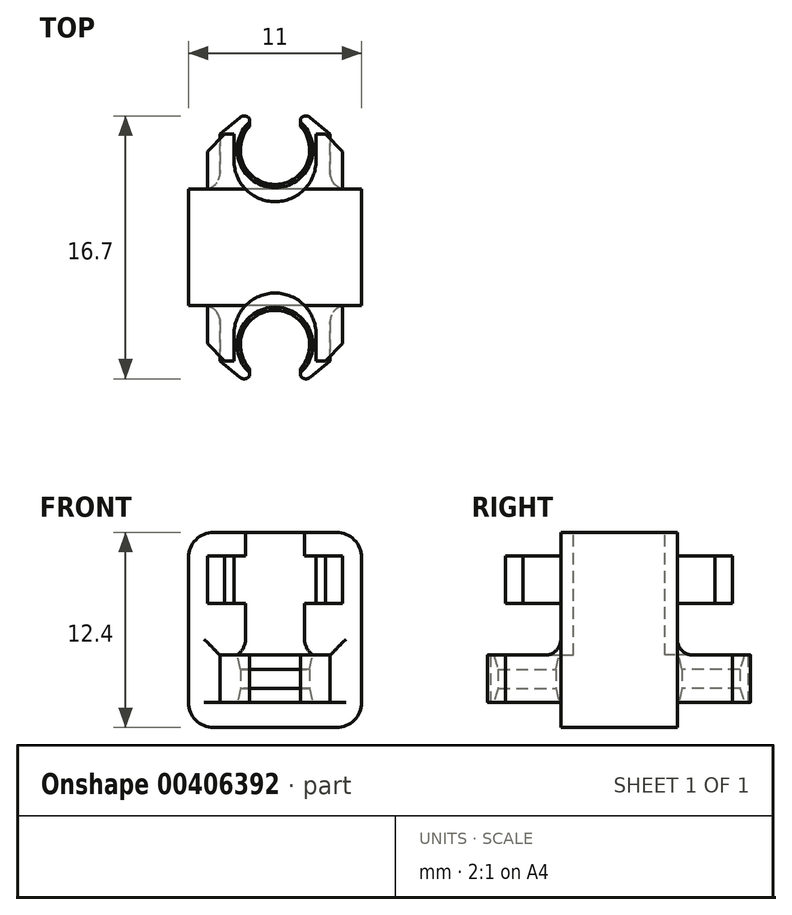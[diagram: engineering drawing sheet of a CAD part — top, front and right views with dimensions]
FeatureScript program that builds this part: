
annotation { "Feature Type Name" : "Feature", "Feature Type Description" : "" }
export const myFeature = defineFeature(function(context is Context, id is Id, definition is map)
    precondition{}
    {
        {
            var Q0;
            Q0=qCreatedBy(makeId("Top.planeOp"),FACE);
            var sketch = newSketch(context, id + "F0", { "sketchPlane" : qUnion([Q0])});
            skArc(sketch, "E0", {"start": v(-1.63, 1.48) * mm, "mid": v(-2.01, -0.9) * mm, "end": v(0, -2.2) * mm});
            skLineSegment(sketch, "E1", {"start": v(-1.63, 1.98) * mm, "end": v(-1.9, 2.31) * mm});
            skLineSegment(sketch, "E2", {"start": v(-1.9, 2.31) * mm, "end": v(-3.5, 1) * mm});
            skLineSegment(sketch, "E3", {"start": v(-5.5, -2.5) * mm, "end": v(-5.5, -6.2) * mm});
            skLineSegment(sketch, "E4", {"start": v(-5.5, -6.2) * mm, "end": v(0, -6.2) * mm});
            skLineSegment(sketch, "E5", {"start": v(0, -6.2) * mm, "end": v(0, -2.2) * mm});
            skLineSegment(sketch, "E6", {"start": v(-3.5, 1) * mm, "end": v(-3.5, -2.5) * mm});
            skLineSegment(sketch, "E7", {"start": v(-3.5, -2.5) * mm, "end": v(-5.5, -2.5) * mm});
            skLineSegment(sketch, "E8", {"start": v(-1.63, 1.98) * mm, "end": v(-1.63, 1.48) * mm});
            skPoint(sketch, "E8.endSnap0", {"position": v(-1.65, 2) * mm});
            skPoint(sketch, "E9.orphan", {"position": v(-1.4, 1.7) * mm});
            skSolve(sketch);
        }
        {
            var Q0;
            Q0 = qSketchRegion(id + "F0", true);
            extrude(context, id + "F1", {"entities" : qUnion([Q0]), "depth" : 12.4 * mm, "offsetDistance" : 25 * mm});
        }
        {
            var Q0;
            Q0=makeQuery(id+"F1.opExtrude","SWEPT_FACE",FACE,{"disambiguationData":[OSD([sQuery(id+"F0.wireOp",EDGE,"E6")])]});
            var sketch = newSketch(context, id + "F2", { "sketchPlane" : qUnion([Q0])});
            skLineSegment(sketch, "E10.bottom", {"start": v(2.5, 7.9) * mm, "end": v(-2.31, 7.9) * mm});
            skLineSegment(sketch, "E10.top", {"start": v(2.5, 4.6) * mm, "end": v(-2.31, 4.6) * mm});
            skLineSegment(sketch, "E10.left", {"start": v(2.5, 7.9) * mm, "end": v(2.5, 4.6) * mm});
            skLineSegment(sketch, "E10.right", {"start": v(-2.31, 7.9) * mm, "end": v(-2.31, 4.6) * mm});
            skLineSegment(sketch, "E11.bottom", {"start": v(-2.31, 0) * mm, "end": v(2.5, 0) * mm});
            skLineSegment(sketch, "E11.top", {"start": v(-2.31, 1.6) * mm, "end": v(2.5, 1.6) * mm});
            skLineSegment(sketch, "E11.left", {"start": v(-2.31, 0) * mm, "end": v(-2.31, 1.6) * mm});
            skLineSegment(sketch, "E11.right", {"start": v(2.5, 0) * mm, "end": v(2.5, 1.6) * mm});
            skLineSegment(sketch, "E12.bottom", {"start": v(2.5, 10.9) * mm, "end": v(-2.31, 10.9) * mm});
            skLineSegment(sketch, "E12.top", {"start": v(2.5, 12.4) * mm, "end": v(-2.31, 12.4) * mm});
            skLineSegment(sketch, "E12.left", {"start": v(2.5, 10.9) * mm, "end": v(2.5, 12.4) * mm});
            skLineSegment(sketch, "E12.right", {"start": v(-2.31, 10.9) * mm, "end": v(-2.31, 12.4) * mm});
            skSolve(sketch);
        }
        {
            var Q0;
            Q0 = qSketchRegion(id + "F2", true);
            extrude(context, id + "F3", {"entities" : qUnion([Q0]), "operationType" : NewBodyOperationType.REMOVE, "oppositeDirection" : true, "depth" : 25 * mm, "offsetDistance" : 25 * mm});
        }
        {
            var Q0;
            Q0=makeQuery(id+"F1.opExtrude","CAP_FACE",FACE,{"disambiguationData":[OSD([sQuery(id+"F0.wireOp",EDGE,"E0"),sQuery(id+"F0.wireOp",EDGE,"E1"),sQuery(id+"F0.wireOp",EDGE,"E2"),sQuery(id+"F0.wireOp",EDGE,"E3"),sQuery(id+"F0.wireOp",EDGE,"E4"),sQuery(id+"F0.wireOp",EDGE,"E5"),sQuery(id+"F0.wireOp",EDGE,"E6"),sQuery(id+"F0.wireOp",EDGE,"E7")])],"isStart":false});
            var sketch = newSketch(context, id + "F4", { "sketchPlane" : qUnion([Q0])});
            skLineSegment(sketch, "E13", {"start": v(-2.6, -0.7) * mm, "end": v(-2.6, 1) * mm});
            skLineSegment(sketch, "E14", {"start": v(-3.5, 1) * mm, "end": v(-2.6, 1) * mm});
            skArc(sketch, "E15", {"start": v(-2.6, -0.7) * mm, "mid": v(-1.84, -2.54) * mm, "end": v(0, -3.3) * mm});
            skLineSegment(sketch, "E16.0", {"start": v(-1.9, 2.31) * mm, "end": v(-3.5, 1) * mm});
            skLineSegment(sketch, "E16.1", {"start": v(-1.63, 1.98) * mm, "end": v(-1.9, 2.31) * mm});
            skLineSegment(sketch, "E17.0", {"start": v(-1.63, 1.98) * mm, "end": v(-1.63, 1.48) * mm});
            skArc(sketch, "E18.0", {"start": v(-1.63, 1.48) * mm, "mid": v(-2.01, -0.9) * mm, "end": v(0, -2.2) * mm});
            skPoint(sketch, "E19.endSnap0", {"position": v(-2.6, 0.15) * mm});
            skLineSegment(sketch, "E20", {"start": v(0, -3.3) * mm, "end": v(0, -2.2) * mm});
            skSolve(sketch);
        }
        {
            var Q0;
            Q0 = qSketchRegion(id + "F4", true);
            var Q1;
            Q1=makeQuery(id+"F3.boolean.opBoolean","COPY",FACE,{"derivedFrom":makeQuery(id+"F3.opExtrude","SWEPT_FACE",FACE,{"disambiguationData":[OSD([sQuery(id+"F2.wireOp",EDGE,"E10.top")])]})});
            extrude(context, id + "F5", {"entities" : qUnion([Q0]), "operationType" : NewBodyOperationType.REMOVE, "endBound" : BoundingType.UP_TO_SURFACE, "oppositeDirection" : true, "depth" : 25 * mm, "endBoundEntityFace" : qUnion([Q1]), "offsetDistance" : 25 * mm});
        }
        {
            var Q0;
            Q0=makeQuery(id+"F3.boolean.opBoolean","SPLIT",FACE,{"disambiguationData":[TD([makeQuery(id+"F3.opExtrude","SWEPT_FACE",FACE,{"disambiguationData":[OSD([sQuery(id+"F2.wireOp",EDGE,"E10.bottom")])]})])],"derivedFrom":makeQuery(id+"F1.opExtrude","SWEPT_FACE",FACE,{"disambiguationData":[OSD([sQuery(id+"F0.wireOp",EDGE,"E6")])]})});
            extrude(context, id + "F6", {"entities" : qUnion([Q0]), "operationType" : NewBodyOperationType.ADD, "depth" : 0.8 * mm, "offsetDistance" : 25 * mm});
        }
        {
            var Q0;
            Q0=makeQuery(id+"F6.opExtrude","CAP_EDGE",EDGE,{"disambiguationData":[OSD([sQuery(id+"F0.wireOp",EDGE,"E2"),sQuery(id+"F0.wireOp",EDGE,"E6"),sQuery(id+"F4.wireOp",EDGE,"E14"),sQuery(id+"F4.wireOp",EDGE,"E16.0")])],"isStart":false});
            chamfer(context, id + "F7", {"entities" : qUnion([Q0]), "width" : 1.1 * mm, "tangentPropagation" : true});
        }
        {
            var Q0;
            {var subQ0=sQuery(id+"F0.wireOp",EDGE,"E2");var subQ1=sQuery(id+"F0.wireOp",EDGE,"E1");Q0=makeQuery(id+"F3.boolean.opBoolean","SPLIT",EDGE,{"disambiguationData":[TD([makeQuery(id+"F3.opExtrude","SWEPT_FACE",FACE,{"disambiguationData":[OSD([sQuery(id+"F2.wireOp",EDGE,"E10.top")])]})])],"derivedFrom":makeQuery(id+"F1.opExtrude","SWEPT_EDGE",EDGE,{"disambiguationData":[OSD([subQ1,subQ0])]})});}
            fillet(context, id + "F8", {"entities" : qUnion([Q0]), "radius" : 0.4 * mm, "tangentPropagation" : true, "allowEdgeOverflow" : false});
        }
        {
            var Q0;
            {var subQ0=sQuery(id+"F0.wireOp",EDGE,"E7");var subQ1=sQuery(id+"F0.wireOp",EDGE,"E6");Q0=makeQuery(id+"F3.boolean.opBoolean","SPLIT",EDGE,{"disambiguationData":[TD([makeQuery(id+"F3.opExtrude","SWEPT_FACE",FACE,{"disambiguationData":[OSD([sQuery(id+"F2.wireOp",EDGE,"E10.top")])]})])],"derivedFrom":makeQuery(id+"F1.opExtrude","SWEPT_EDGE",EDGE,{"disambiguationData":[OSD([subQ1,subQ0])]})});}
            var Q1;
            {var subQ0=sQuery(id+"F0.wireOp",EDGE,"E7");var subQ1=sQuery(id+"F0.wireOp",EDGE,"E6");Q1=makeQuery(id+"F3.boolean.opBoolean","SPLIT",EDGE,{"disambiguationData":[TD([makeQuery(id+"F3.opExtrude","SWEPT_FACE",FACE,{"disambiguationData":[OSD([sQuery(id+"F2.wireOp",EDGE,"E10.bottom")])]})])],"derivedFrom":makeQuery(id+"F1.opExtrude","SWEPT_EDGE",EDGE,{"disambiguationData":[OSD([subQ1,subQ0])]})});}
            var Q2;
            Q2=makeQuery(id+"F3.boolean.opBoolean","COPY",EDGE,{"derivedFrom":makeQuery(id+"F3.opExtrude","SWEPT_EDGE",EDGE,{"disambiguationData":[OSD([sQuery(id+"F0.wireOp",EDGE,"E6"),sQuery(id+"F0.wireOp",EDGE,"E7"),sQuery(id+"F2.wireOp",EDGE,"E10.top"),sQuery(id+"F2.wireOp",EDGE,"E10.left")])]})});
            var Q3;
            Q3=makeQuery(id+"F3.boolean.opBoolean","COPY",EDGE,{"derivedFrom":makeQuery(id+"F3.opExtrude","SWEPT_EDGE",EDGE,{"disambiguationData":[OSD([sQuery(id+"F0.wireOp",EDGE,"E6"),sQuery(id+"F0.wireOp",EDGE,"E7"),sQuery(id+"F2.wireOp",EDGE,"E10.bottom"),sQuery(id+"F2.wireOp",EDGE,"E10.left")])]})});
            var Q4;
            Q4=makeQuery(id+"F6.opExtrude","CAP_EDGE",EDGE,{"disambiguationData":[OSD([sQuery(id+"F0.wireOp",EDGE,"E6"),sQuery(id+"F0.wireOp",EDGE,"E7")])],"isStart":false});
            fillet(context, id + "F9", {"entities" : qUnion([Q0, Q1, Q2, Q3, Q4]), "radius" : 1 * mm, "tangentPropagation" : true, "allowEdgeOverflow" : false});
        }
        {
            var Q0;
            Q0=makeQuery(id+"F3.boolean.opBoolean","INTERSECT",EDGE,{"derivedFrom":[makeQuery(id+"F1.opExtrude","SWEPT_FACE",FACE,{"disambiguationData":[OSD([sQuery(id+"F0.wireOp",EDGE,"E0")])]}),makeQuery(id+"F3.opExtrude","SWEPT_FACE",FACE,{"disambiguationData":[OSD([sQuery(id+"F2.wireOp",EDGE,"E11.top")])]})]});
            var Q1;
            Q1=makeQuery(id+"F3.boolean.opBoolean","INTERSECT",EDGE,{"derivedFrom":[makeQuery(id+"F1.opExtrude","SWEPT_FACE",FACE,{"disambiguationData":[OSD([sQuery(id+"F0.wireOp",EDGE,"E0")])]}),makeQuery(id+"F3.opExtrude","SWEPT_FACE",FACE,{"disambiguationData":[OSD([sQuery(id+"F2.wireOp",EDGE,"E10.top")])]})]});
            chamfer(context, id + "F10", {"entities" : qUnion([Q0, Q1]), "chamferType" : ChamferType.TWO_OFFSETS, "width1" : 0.2 * mm, "oppositeDirection" : true, "width2" : 0.9 * mm, "tangentPropagation" : true});
        }
        {
            var Q0;
            Q0=makeQuery(id+"F1.opExtrude","SWEPT_BODY",BODY,{"disambiguationData":[OSD([sQuery(id+"F0.wireOp",EDGE,"E0"),sQuery(id+"F0.wireOp",EDGE,"E1"),sQuery(id+"F0.wireOp",EDGE,"E2"),sQuery(id+"F0.wireOp",EDGE,"E3"),sQuery(id+"F0.wireOp",EDGE,"E4"),sQuery(id+"F0.wireOp",EDGE,"E5"),sQuery(id+"F0.wireOp",EDGE,"E6"),sQuery(id+"F0.wireOp",EDGE,"E7")])]});
            var Q1;
            Q1=makeQuery(id+"F1.opExtrude","SWEPT_FACE",FACE,{"disambiguationData":[OSD([sQuery(id+"F0.wireOp",EDGE,"E5")])]});
            mirror(context, id + "F11", {"operationType" : NewBodyOperationType.ADD, "entities" : qUnion([Q0]), "mirrorPlane" : qUnion([Q1])});
        }
        {
            var Q0;
            Q0=makeQuery(id+"F1.opExtrude","SWEPT_BODY",BODY,{"disambiguationData":[OSD([sQuery(id+"F0.wireOp",EDGE,"E0"),sQuery(id+"F0.wireOp",EDGE,"E1"),sQuery(id+"F0.wireOp",EDGE,"E2"),sQuery(id+"F0.wireOp",EDGE,"E3"),sQuery(id+"F0.wireOp",EDGE,"E4"),sQuery(id+"F0.wireOp",EDGE,"E5"),sQuery(id+"F0.wireOp",EDGE,"E6"),sQuery(id+"F0.wireOp",EDGE,"E7")])]});
            var Q1;
            {var subQ0=makeQuery(id+"F1.opExtrude","SWEPT_FACE",FACE,{"disambiguationData":[OSD([sQuery(id+"F0.wireOp",EDGE,"E4")])]});Q1=makeQuery(id+"F11.boolean.opBoolean","MERGE",FACE,{"derivedFrom":[subQ0,makeQuery(id+"F11.opPattern","COPY",FACE,{"derivedFrom":subQ0,"instanceName":"1"})]});}
            mirror(context, id + "F12", {"operationType" : NewBodyOperationType.ADD, "entities" : qUnion([Q0]), "mirrorPlane" : qUnion([Q1])});
        }
        {
            var Q0;
            {var subQ0=makeQuery(id+"F11.opPattern","COPY",EDGE,{"derivedFrom":makeQuery(id+"F1.opExtrude","CAP_EDGE",EDGE,{"disambiguationData":[OSD([sQuery(id+"F0.wireOp",EDGE,"E3")])],"isStart":true}),"instanceName":"1"});Q0=makeQuery(id+"F12.boolean.opBoolean","MERGE",EDGE,{"derivedFrom":[subQ0,makeQuery(id+"F12.opPattern","COPY",EDGE,{"derivedFrom":subQ0,"instanceName":"1"})]});}
            var Q1;
            {var subQ0=makeQuery(id+"F1.opExtrude","CAP_EDGE",EDGE,{"disambiguationData":[OSD([sQuery(id+"F0.wireOp",EDGE,"E3")])],"isStart":true});Q1=makeQuery(id+"F12.boolean.opBoolean","MERGE",EDGE,{"derivedFrom":[subQ0,makeQuery(id+"F12.opPattern","COPY",EDGE,{"derivedFrom":subQ0,"instanceName":"1"})]});}
            var Q2;
            {var subQ0=makeQuery(id+"F11.opPattern","COPY",EDGE,{"derivedFrom":makeQuery(id+"F1.opExtrude","CAP_EDGE",EDGE,{"disambiguationData":[OSD([sQuery(id+"F0.wireOp",EDGE,"E3")])],"isStart":false}),"instanceName":"1"});Q2=makeQuery(id+"F12.boolean.opBoolean","MERGE",EDGE,{"derivedFrom":[subQ0,makeQuery(id+"F12.opPattern","COPY",EDGE,{"derivedFrom":subQ0,"instanceName":"1"})]});}
            var Q3;
            {var subQ0=makeQuery(id+"F1.opExtrude","CAP_EDGE",EDGE,{"disambiguationData":[OSD([sQuery(id+"F0.wireOp",EDGE,"E3")])],"isStart":false});Q3=makeQuery(id+"F12.boolean.opBoolean","MERGE",EDGE,{"derivedFrom":[subQ0,makeQuery(id+"F12.opPattern","COPY",EDGE,{"derivedFrom":subQ0,"instanceName":"1"})]});}
            fillet(context, id + "F14", {"entities" : qUnion([Q0, Q1, Q2, Q3]), "radius" : 1.6 * mm, "tangentPropagation" : true, "allowEdgeOverflow" : false});
        }
    });
